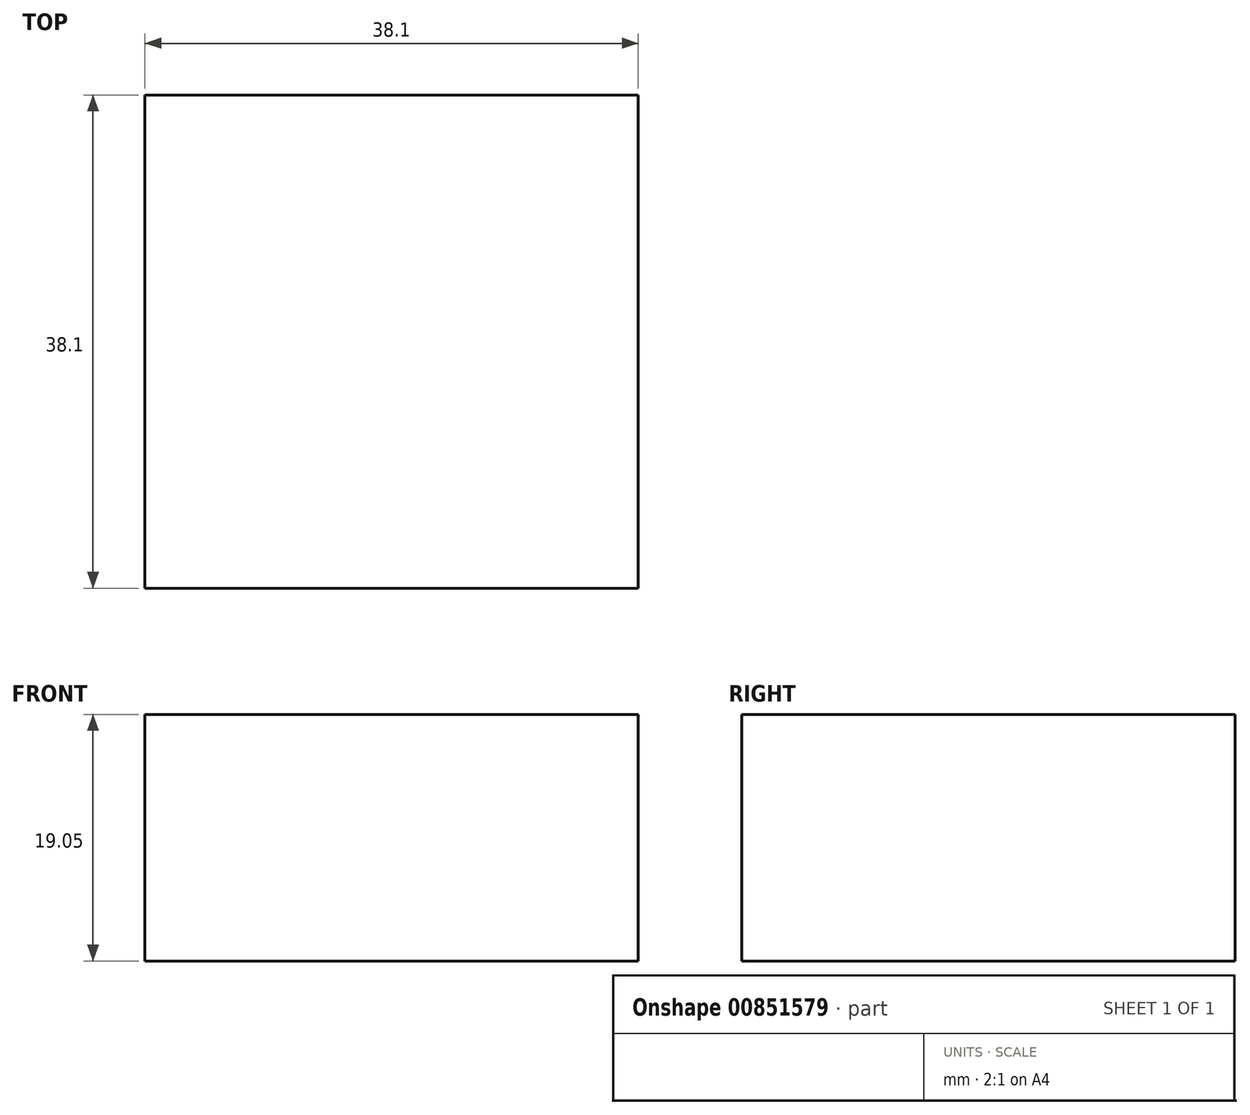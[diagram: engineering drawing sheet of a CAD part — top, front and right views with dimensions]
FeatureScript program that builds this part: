
annotation { "Feature Type Name" : "Feature", "Feature Type Description" : "" }
export const myFeature = defineFeature(function(context is Context, id is Id, definition is map)
    precondition{}
    {
        {
            var Q0;
            Q0=qCreatedBy(makeId("Top.planeOp"),FACE);
            var sketch = newSketch(context, id + "F0", { "sketchPlane" : qUnion([Q0])});
            skLineSegment(sketch, "E0.bottom", {"start": v(19.05, 19.05) * mm, "end": v(-19.05, 19.05) * mm});
            skLineSegment(sketch, "E0.top", {"start": v(19.05, -19.05) * mm, "end": v(-19.05, -19.05) * mm});
            skLineSegment(sketch, "E0.left", {"start": v(19.05, 19.05) * mm, "end": v(19.05, -19.05) * mm});
            skLineSegment(sketch, "E0.right", {"start": v(-19.05, 19.05) * mm, "end": v(-19.05, -19.05) * mm});
            skPoint(sketch, "E0.middle", {"position": v(0, 0) * mm});
            skSolve(sketch);
        }
        {
            var Q0;
            Q0=makeQuery(id+"F0.imprint","IMPRINT",FACE,{"disambiguationData":[TD([[makeQuery(id+"F0.imprint","IMPRINT",EDGE,{"derivedFrom":sQuery(id+"F0.wireOp",EDGE,"E0.bottom")}),1.0]])]});
            extrude(context, id + "F1", {"entities" : qUnion([Q0]), "depth" : 19.05 * mm, "offsetDistance" : 25.4 * mm});
        }
    });
